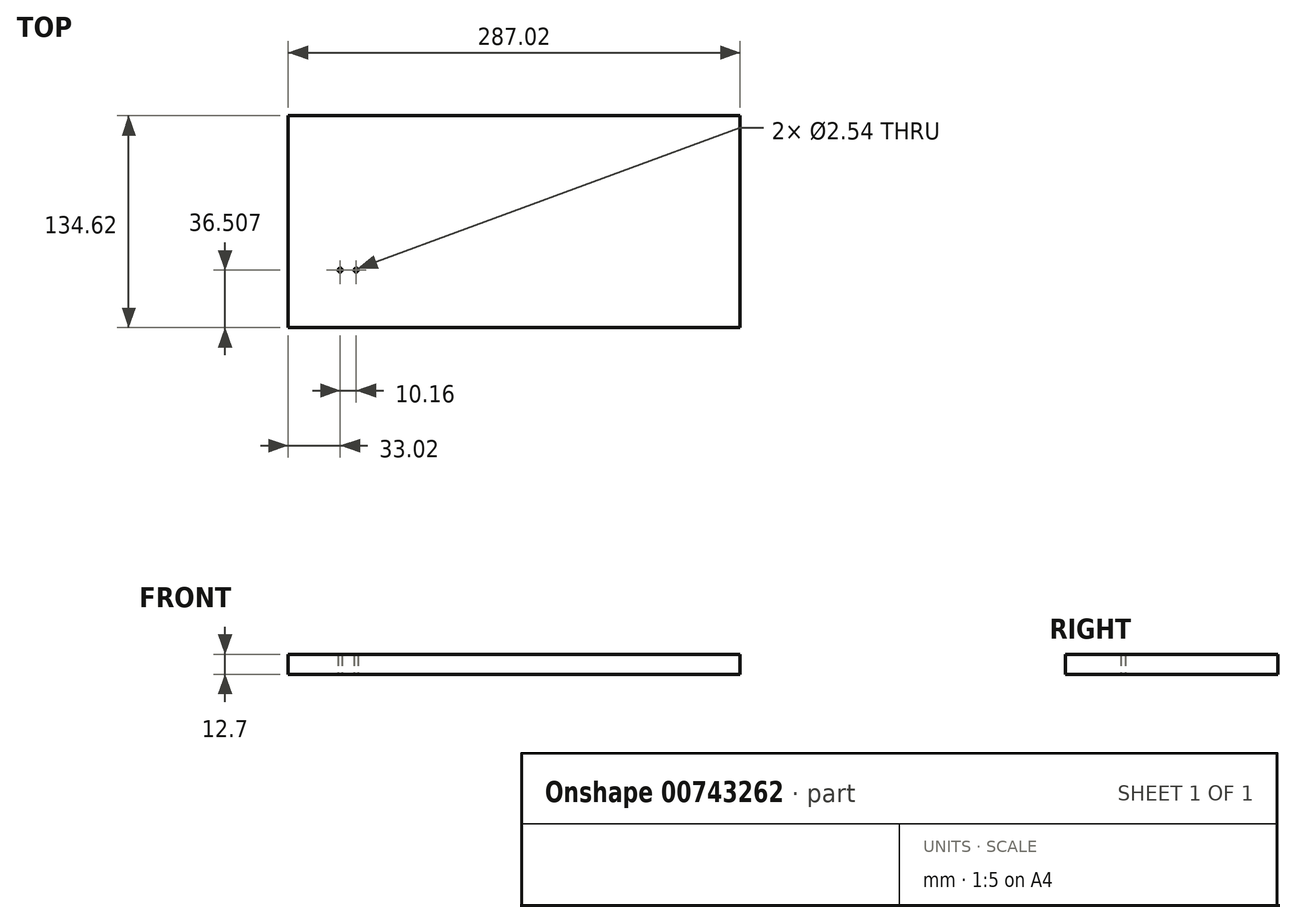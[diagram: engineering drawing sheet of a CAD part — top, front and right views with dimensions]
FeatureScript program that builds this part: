
annotation { "Feature Type Name" : "Feature", "Feature Type Description" : "" }
export const myFeature = defineFeature(function(context is Context, id is Id, definition is map)
    precondition{}
    {
        {
            var Q0;
            Q0=qCreatedBy(makeId("Top.planeOp"),FACE);
            var sketch = newSketch(context, id + "F0", { "sketchPlane" : qUnion([Q0])});
            skLineSegment(sketch, "E0.bottom", {"start": v(143.51, 67.31) * mm, "end": v(-143.51, 67.31) * mm});
            skLineSegment(sketch, "E0.top", {"start": v(143.5, -67.31) * mm, "end": v(-143.51, -67.31) * mm});
            skLineSegment(sketch, "E0.left", {"start": v(143.51, 67.31) * mm, "end": v(143.5, -67.31) * mm});
            skLineSegment(sketch, "E0.right", {"start": v(-143.51, 67.31) * mm, "end": v(-143.51, -67.31) * mm});
            skPoint(sketch, "E0.middle", {"position": v(0, 0) * mm});
            skLineSegment(sketch, "E1.bottom", {"start": v(105.41, -30.8) * mm, "end": v(-105.41, -30.8) * mm, "construction": true});
            skLineSegment(sketch, "E1.top", {"start": v(105.41, -24.45) * mm, "end": v(-105.41, -24.45) * mm, "construction": true});
            skLineSegment(sketch, "E1.left", {"start": v(105.41, -30.8) * mm, "end": v(105.41, -24.45) * mm, "construction": true});
            skLineSegment(sketch, "E1.right", {"start": v(-105.41, -30.8) * mm, "end": v(-105.41, -24.45) * mm, "construction": true});
            skPoint(sketch, "E1.middle", {"position": v(0, -27.63) * mm});
            skCircle(sketch, "E2", {"center": v(-100.33, -30.8) * mm, "radius": 1.27 * mm});
            skCircle(sketch, "E3", {"center": v(-110.5, -30.8) * mm, "radius": 1.27 * mm});
            skLineSegment(sketch, "E4", {"start": v(0, -24.45) * mm, "end": v(0, -30.8) * mm});
            skSolve(sketch);
        }
        {
            var Q0;
            Q0=makeQuery(id+"F0.imprint","IMPRINT",FACE,{"disambiguationData":[TD([[makeQuery(id+"F0.imprint","IMPRINT",EDGE,{"derivedFrom":sQuery(id+"F0.wireOp",EDGE,"E0.bottom")}),1.0]])]});
            extrude(context, id + "F1", {"entities" : qUnion([Q0]), "depth" : 12.7 * mm, "offsetDistance" : 25.4 * mm});
        }
    });
